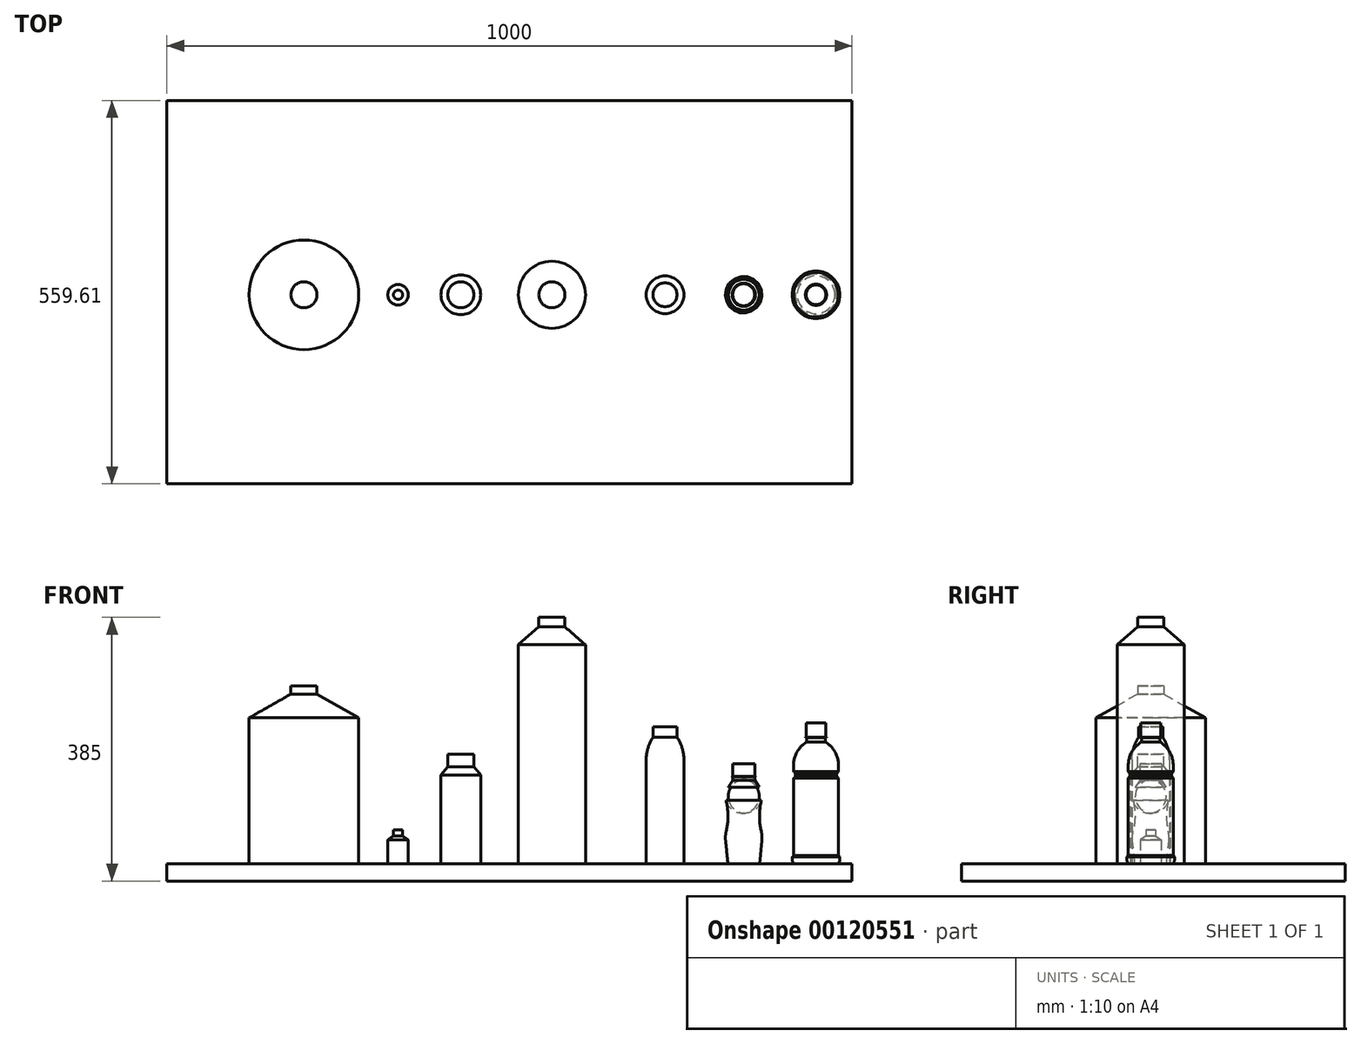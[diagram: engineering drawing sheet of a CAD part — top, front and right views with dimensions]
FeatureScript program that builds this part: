
annotation { "Feature Type Name" : "Feature", "Feature Type Description" : "" }
export const myFeature = defineFeature(function(context is Context, id is Id, definition is map)
    precondition{}
    {
        {
            var Q0;
            Q0=qCreatedBy(makeId("Front.planeOp"),FACE);
            var sketch = newSketch(context, id + "F0", { "sketchPlane" : qUnion([Q0])});
            skLineSegment(sketch, "E0", {"start": v(29, 160) * mm, "end": v(29, 0) * mm});
            skLineSegment(sketch, "E1", {"start": v(48, 160) * mm, "end": v(48, 142) * mm});
            skLineSegment(sketch, "E2", {"start": v(48, 142) * mm, "end": v(58, 130) * mm});
            skLineSegment(sketch, "E3", {"start": v(29, 160) * mm, "end": v(48, 160) * mm});
            skLineSegment(sketch, "E4", {"start": v(58, 130) * mm, "end": v(58, 0) * mm});
            skLineSegment(sketch, "E5", {"start": v(29, 0) * mm, "end": v(58, 0) * mm});
            skSolve(sketch);
        }
        {
            var Q0;
            Q0=makeQuery(id+"F0.imprint","IMPRINT",FACE,{"disambiguationData":[TD([[makeQuery(id+"F0.imprint","IMPRINT",EDGE,{"derivedFrom":sQuery(id+"F0.wireOp",EDGE,"E0")}),1.0]])]});
            var Q1;
            Q1=sQuery(id+"F0.wireOp",EDGE,"E0");
            revolve(context, id + "F1", {"entities" : qUnion([Q0]), "axis" : qUnion([Q1]), "revolveType" : RevolveType.ONE_DIRECTION, "angle" : 360 * degree});
        }
        {
            var Q0;
            Q0=qCreatedBy(makeId("Front.planeOp"),FACE);
            var sketch = newSketch(context, id + "F2", { "sketchPlane" : qUnion([Q0])});
            skLineSegment(sketch, "E6", {"start": v(161.94, 360) * mm, "end": v(161.94, 0) * mm});
            skLineSegment(sketch, "E7", {"start": v(161.94, 360) * mm, "end": v(142.94, 360) * mm});
            skLineSegment(sketch, "E8", {"start": v(142.94, 360) * mm, "end": v(142.94, 346) * mm});
            skLineSegment(sketch, "E9", {"start": v(142.94, 346) * mm, "end": v(112.94, 320) * mm});
            skLineSegment(sketch, "E10", {"start": v(112.94, 320) * mm, "end": v(112.94, 0) * mm});
            skLineSegment(sketch, "E11", {"start": v(112.94, 0) * mm, "end": v(161.94, 0) * mm});
            skSolve(sketch);
        }
        {
            var Q0;
            Q0=makeQuery(id+"F2.imprint","IMPRINT",FACE,{"disambiguationData":[TD([[makeQuery(id+"F2.imprint","IMPRINT",EDGE,{"derivedFrom":sQuery(id+"F2.wireOp",EDGE,"E6")}),-1.0]])]});
            var Q1;
            Q1=sQuery(id+"F2.wireOp",EDGE,"E6");
            revolve(context, id + "F3", {"entities" : qUnion([Q0]), "axis" : qUnion([Q1]), "revolveType" : RevolveType.FULL});
        }
        {
            var Q0;
            Q0=qCreatedBy(makeId("Front.planeOp"),FACE);
            var sketch = newSketch(context, id + "F4", { "sketchPlane" : qUnion([Q0])});
            skLineSegment(sketch, "E12", {"start": v(-280, 0) * mm, "end": v(-200, 0) * mm});
            skLineSegment(sketch, "E13", {"start": v(-200, 0) * mm, "end": v(-200, 260) * mm});
            skLineSegment(sketch, "E14", {"start": v(-200, 260) * mm, "end": v(-219, 260) * mm});
            skLineSegment(sketch, "E15", {"start": v(-219, 260) * mm, "end": v(-219, 248) * mm});
            skLineSegment(sketch, "E16", {"start": v(-219, 248) * mm, "end": v(-280, 213.3) * mm});
            skLineSegment(sketch, "E17", {"start": v(-280, 213.3) * mm, "end": v(-280, 0) * mm});
            skSolve(sketch);
        }
        {
            var Q0;
            Q0=makeQuery(id+"F4.imprint","IMPRINT",FACE,{"disambiguationData":[TD([[makeQuery(id+"F4.imprint","IMPRINT",EDGE,{"derivedFrom":sQuery(id+"F4.wireOp",EDGE,"E12")}),1.0]])]});
            var Q1;
            Q1=sQuery(id+"F4.wireOp",EDGE,"E13");
            revolve(context, id + "F5", {"entities" : qUnion([Q0]), "axis" : qUnion([Q1]), "revolveType" : RevolveType.FULL});
        }
        {
            var Q0;
            Q0=qCreatedBy(makeId("Front.planeOp"),FACE);
            var sketch = newSketch(context, id + "F6", { "sketchPlane" : qUnion([Q0])});
            skLineSegment(sketch, "E18", {"start": v(-62.63, 0) * mm, "end": v(-62.63, 50) * mm});
            skLineSegment(sketch, "E19", {"start": v(-62.63, 50) * mm, "end": v(-69.36, 50) * mm});
            skLineSegment(sketch, "E20", {"start": v(-69.36, 50) * mm, "end": v(-69.36, 41) * mm});
            skLineSegment(sketch, "E21", {"start": v(-69.36, 41) * mm, "end": v(-77.63, 35) * mm});
            skLineSegment(sketch, "E22", {"start": v(-77.63, 35) * mm, "end": v(-77.63, 0) * mm});
            skLineSegment(sketch, "E23", {"start": v(-77.63, 0) * mm, "end": v(-62.63, 0) * mm});
            skSolve(sketch);
        }
        {
            var Q0;
            Q0=makeQuery(id+"F6.imprint","IMPRINT",FACE,{"disambiguationData":[TD([[makeQuery(id+"F6.imprint","IMPRINT",EDGE,{"derivedFrom":sQuery(id+"F6.wireOp",EDGE,"E18")}),1.0]])]});
            var Q1;
            Q1=sQuery(id+"F6.wireOp",EDGE,"E18");
            revolve(context, id + "F7", {"entities" : qUnion([Q0]), "axis" : qUnion([Q1]), "revolveType" : RevolveType.FULL});
        }
        {
            var Q0;
            Q0=qCreatedBy(makeId("Front.planeOp"),FACE);
            var sketch = newSketch(context, id + "F8", { "sketchPlane" : qUnion([Q0])});
            skLineSegment(sketch, "E24.bottom", {"start": v(299.6, 0) * mm, "end": v(327.1, 0) * mm});
            skLineSegment(sketch, "E24.left", {"start": v(299.6, 0) * mm, "end": v(299.6, 152) * mm});
            skLineSegment(sketch, "E24.right", {"start": v(327.1, 0) * mm, "end": v(327.1, 200) * mm});
            skLineSegment(sketch, "E25", {"start": v(327.1, 200) * mm, "end": v(309.6, 200) * mm});
            skLineSegment(sketch, "E26", {"start": v(309.6, 200) * mm, "end": v(309.6, 185) * mm});
            skArc(sketch, "E27", {"start": v(309.6, 185) * mm, "mid": v(302.16, 169.24) * mm, "end": v(299.6, 152) * mm});
            skSolve(sketch);
        }
        {
            var Q0;
            Q0 = qSketchRegion(id + "F8", true);
            var Q1;
            Q1=sQuery(id+"F8.wireOp",EDGE,"E24.right");
            revolve(context, id + "F9", {"entities" : qUnion([Q0]), "axis" : qUnion([Q1]), "revolveType" : RevolveType.FULL});
        }
        {
            var Q0;
            Q0=qCreatedBy(makeId("Top.planeOp"),FACE);
            var sketch = newSketch(context, id + "F10", { "sketchPlane" : qUnion([Q0])});
            skLineSegment(sketch, "E28.bottom", {"start": v(-400, 283.57) * mm, "end": v(600, 283.57) * mm});
            skLineSegment(sketch, "E28.top", {"start": v(-400, -276.04) * mm, "end": v(600, -276.04) * mm});
            skLineSegment(sketch, "E28.left", {"start": v(-400, 283.57) * mm, "end": v(-400, -276.04) * mm});
            skLineSegment(sketch, "E28.right", {"start": v(600, 283.57) * mm, "end": v(600, -276.04) * mm});
            skSolve(sketch);
        }
        {
            var Q0;
            Q0=qCreatedBy(makeId("Front.planeOp"),FACE);
            var sketch = newSketch(context, id + "F11", { "sketchPlane" : qUnion([Q0])});
            skLineSegment(sketch, "E29", {"start": v(418.95, 0) * mm, "end": v(441.95, 0) * mm});
            skLineSegment(sketch, "E30", {"start": v(441.95, 0) * mm, "end": v(441.95, 146) * mm});
            skLineSegment(sketch, "E31", {"start": v(441.95, 146) * mm, "end": v(425.95, 146) * mm});
            skLineSegment(sketch, "E32", {"start": v(425.95, 146) * mm, "end": v(425.95, 128) * mm});
            skLineSegment(sketch, "E33", {"start": v(425.95, 128) * mm, "end": v(424.95, 128) * mm});
            skLineSegment(sketch, "E34", {"start": v(424.95, 128) * mm, "end": v(424.95, 127) * mm});
            skLineSegment(sketch, "E35", {"start": v(424.95, 127) * mm, "end": v(425.95, 127) * mm});
            skLineSegment(sketch, "E36", {"start": v(425.95, 127) * mm, "end": v(425.95, 122) * mm});
            skLineSegment(sketch, "E37", {"start": v(418.95, 0) * mm, "end": v(415.45, 34) * mm});
            skLineSegment(sketch, "E38", {"start": v(425.95, 122) * mm, "end": v(419.41, 111.94) * mm});
            skArc(sketch, "E39", {"start": v(419.41, 111.94) * mm, "mid": v(415.79, 102.63) * mm, "end": v(416.17, 92.65) * mm});
            skArc(sketch, "E40", {"start": v(416.36, 47.81) * mm, "mid": v(418.95, 70.24) * mm, "end": v(416.17, 92.65) * mm});
            skArc(sketch, "E41", {"start": v(416.36, 47.81) * mm, "mid": v(415.32, 40.94) * mm, "end": v(415.45, 34) * mm});
            skSolve(sketch);
        }
        {
            var Q0;
            Q0 = qSketchRegion(id + "F11", true);
            var Q1;
            Q1=sQuery(id+"F11.wireOp",EDGE,"E30");
            revolve(context, id + "F12", {"entities" : qUnion([Q0]), "axis" : qUnion([Q1]), "revolveType" : RevolveType.FULL});
        }
        {
            var Q0;
            Q0=qCreatedBy(makeId("Front.planeOp"),FACE);
            var sketch = newSketch(context, id + "F13", { "sketchPlane" : qUnion([Q0])});
            skLineSegment(sketch, "E42", {"start": v(520, 0) * mm, "end": v(547.5, 0) * mm});
            skLineSegment(sketch, "E43", {"start": v(547.5, 0) * mm, "end": v(547.5, 206) * mm});
            skLineSegment(sketch, "E44", {"start": v(547.5, 206) * mm, "end": v(533, 206) * mm});
            skLineSegment(sketch, "E45", {"start": v(533, 206) * mm, "end": v(533, 185) * mm});
            skLineSegment(sketch, "E46", {"start": v(533, 185) * mm, "end": v(532, 185) * mm});
            skLineSegment(sketch, "E47", {"start": v(532, 185) * mm, "end": v(532, 184) * mm});
            skLineSegment(sketch, "E48", {"start": v(532, 184) * mm, "end": v(534, 184) * mm});
            skLineSegment(sketch, "E49", {"start": v(534, 184) * mm, "end": v(534, 178) * mm});
            skArc(sketch, "E50", {"start": v(512.7, 6) * mm, "mid": v(514.93, 1.28) * mm, "end": v(520, 0) * mm});
            skLineSegment(sketch, "E51", {"start": v(514.7, 125) * mm, "end": v(517.2, 127.5) * mm});
            skLineSegment(sketch, "E52", {"start": v(517.2, 127.5) * mm, "end": v(517.2, 132.5) * mm});
            skLineSegment(sketch, "E53", {"start": v(517.2, 132.5) * mm, "end": v(514.7, 135) * mm});
            skLineSegment(sketch, "E54", {"start": v(514.7, 135) * mm, "end": v(514.7, 144) * mm});
            skArc(sketch, "E55", {"start": v(534, 178) * mm, "mid": v(519.86, 163.55) * mm, "end": v(514.7, 144) * mm});
            skLineSegment(sketch, "E56", {"start": v(512.7, 6) * mm, "end": v(512.7, 10) * mm});
            skLineSegment(sketch, "E57", {"start": v(512.7, 10) * mm, "end": v(514.7, 12) * mm});
            skLineSegment(sketch, "E58", {"start": v(514.7, 12) * mm, "end": v(514.7, 125) * mm});
            skSolve(sketch);
        }
        {
            var Q0;
            Q0 = qSketchRegion(id + "F13", true);
            var Q1;
            Q1=sQuery(id+"F13.wireOp",EDGE,"E43");
            revolve(context, id + "F14", {"entities" : qUnion([Q0]), "axis" : qUnion([Q1]), "revolveType" : RevolveType.FULL});
        }
        {
            var Q0;
            Q0=makeQuery(id+"F10.imprint","IMPRINT",FACE,{"disambiguationData":[TD([[makeQuery(id+"F10.imprint","IMPRINT",EDGE,{"derivedFrom":sQuery(id+"F10.wireOp",EDGE,"E28.bottom")}),-1.0]])]});
            var Q1;
            Q1 = qSketchRegion(id + "F10", true);
            extrude(context, id + "F15", {"entities" : qUnion([Q0, Q1]), "oppositeDirection" : true, "depth" : 25 * mm});
        }
    });
